annotation { "Feature Type Name" : "Feature", "Feature Type Description" : "" }
export const myFeature = defineFeature(function(context is Context, id is Id, definition is map)
    precondition{}
    {
        {
            var Q0;
            Q0=qCreatedBy(makeId("Top.planeOp"),FACE);
            var sketch = newSketch(context, id + "F0", { "sketchPlane" : qUnion([Q0])});
            skCircle(sketch, "E0", {"center": v(0, 0) * mm, "radius": 11 * mm});
            skCircle(sketch, "E1", {"center": v(0, 0) * mm, "radius": 13 * mm});
            skLineSegment(sketch, "E2", {"start": v(0, 0) * mm, "end": v(-13, 0) * mm});
            skArc(sketch, "E3", {"start": v(-13, 0) * mm, "mid": v(-12.77, 6.14) * mm, "end": v(-12.93, 12.28) * mm});
            skArc(sketch, "E4.MirrorCS", {"start": v(6.47, 11.28) * mm, "mid": v(1.06, 14.14) * mm, "end": v(-4.16, 17.34) * mm});
            skArc(sketch, "E5.1.0", {"start": v(6.5, -11.25) * mm, "mid": v(1.07, -14.12) * mm, "end": v(-4.17, -17.33) * mm});
            skArc(sketch, "E5.1.1", {"start": v(-13, -0.03) * mm, "mid": v(-12.78, -6.15) * mm, "end": v(-12.93, -12.28) * mm});
            skArc(sketch, "E5.2.0", {"start": v(6.5, 11.26) * mm, "mid": v(11.7, 7.99) * mm, "end": v(17.1, 5.05) * mm});
            skArc(sketch, "E5.2.1", {"start": v(6.53, -11.24) * mm, "mid": v(11.72, -7.98) * mm, "end": v(17.1, -5.05) * mm});
            skArc(sketch, "E6", {"start": v(-4.16, 17.34) * mm, "mid": v(-1.68, 23.22) * mm, "end": v(-2.3, 29.57) * mm});
            skCircle(sketch, "E7", {"center": v(-14.53, 25.18) * mm, "radius": 11 * mm});
            skCircle(sketch, "E8.1.0", {"center": v(-14.53, -25.18) * mm, "radius": 11 * mm});
            skArc(sketch, "E8.1.1", {"start": v(-12.93, -12.28) * mm, "mid": v(-19.27, -13.08) * mm, "end": v(-24.46, -16.8) * mm});
            skCircle(sketch, "E8.2.0", {"center": v(29.08, 0) * mm, "radius": 11 * mm});
            skArc(sketch, "E8.2.1", {"start": v(17.1, -5.05) * mm, "mid": v(20.95, -10.15) * mm, "end": v(26.76, -12.8) * mm});
            skPoint(sketch, "E9.orphan", {"position": v(-14.54, -25.16) * mm});
            skPoint(sketch, "E10.orphan", {"position": v(-14.55, -25.2) * mm});
            skPoint(sketch, "E11.orphan", {"position": v(-14.54, -25.18) * mm});
            skPoint(sketch, "E12.orphan", {"position": v(13, 0) * mm});
            skPoint(sketch, "E13.orphan", {"position": v(29.06, 0) * mm});
            skPoint(sketch, "E14.orphan", {"position": v(29.1, 0.02) * mm});
            skPoint(sketch, "E15.orphan", {"position": v(-6.5, 11.26) * mm});
            skPoint(sketch, "E16.orphan", {"position": v(-14.57, 25.2) * mm});
            skLineSegment(sketch, "E17", {"start": v(-14.53, 25.18) * mm, "end": v(-27.53, 25.18) * mm});
            skLineSegment(sketch, "E18", {"start": v(-27.53, 25.18) * mm, "end": v(-27.53, -25.18) * mm});
            skLineSegment(sketch, "E19", {"start": v(-24.46, 16.79) * mm, "end": v(-24.46, -16.8) * mm});
            skLineSegment(sketch, "E20.1.0", {"start": v(-8.04, -36.43) * mm, "end": v(35.57, -11.25) * mm});
            skLineSegment(sketch, "E20.1.1", {"start": v(-2.3, -29.58) * mm, "end": v(26.77, -12.79) * mm});
            skLineSegment(sketch, "E20.2.0", {"start": v(35.57, 11.25) * mm, "end": v(-8.04, 36.43) * mm});
            skLineSegment(sketch, "E20.2.1", {"start": v(26.77, 12.79) * mm, "end": v(-2.3, 29.57) * mm});
            skArc(sketch, "E21.trimOffspring", {"start": v(-24.46, 16.79) * mm, "mid": v(-19.26, 13.07) * mm, "end": v(-12.93, 12.28) * mm});
            skArc(sketch, "E22.trimOffspring", {"start": v(-27.53, -25.18) * mm, "mid": v(-20.78, -36.58) * mm, "end": v(-7.54, -36.14) * mm});
            skArc(sketch, "E23.trimOffspring", {"start": v(-2.3, -29.57) * mm, "mid": v(-1.68, -23.2) * mm, "end": v(-4.17, -17.33) * mm});
            skArc(sketch, "E24.trimOffspring", {"start": v(35.07, -11.54) * mm, "mid": v(42.08, -0.06) * mm, "end": v(35.17, 11.48) * mm});
            skArc(sketch, "E25.trimOffspring", {"start": v(26.77, 12.79) * mm, "mid": v(20.96, 10.14) * mm, "end": v(17.1, 5.05) * mm});
            skArc(sketch, "E26.trimOffspring", {"start": v(-7.63, 36.2) * mm, "mid": v(-20.83, 36.55) * mm, "end": v(-27.53, 25.18) * mm});
            skPoint(sketch, "E27.orphan", {"position": v(-2.31, 29.58) * mm});
            skCircle(sketch, "E28.cCircle", {"center": v(-14.53, -25.18) * mm, "radius": 6.35 * mm, "construction": true});
            skLineSegment(sketch, "E28.0", {"start": v(-14.82, -17.86) * mm, "end": v(-8.33, -21.27) * mm});
            skLineSegment(sketch, "E28.1", {"start": v(-8.33, -21.27) * mm, "end": v(-8.04, -28.6) * mm});
            skLineSegment(sketch, "E28.2", {"start": v(-8.04, -28.6) * mm, "end": v(-14.24, -32.51) * mm});
            skLineSegment(sketch, "E28.3", {"start": v(-14.24, -32.51) * mm, "end": v(-20.73, -29.1) * mm});
            skLineSegment(sketch, "E28.4", {"start": v(-20.73, -29.1) * mm, "end": v(-21.02, -21.77) * mm});
            skLineSegment(sketch, "E28.5", {"start": v(-21.02, -21.77) * mm, "end": v(-14.82, -17.86) * mm});
            skPoint(sketch, "E28.0.midPoint", {"position": v(-11.57, -19.56) * mm});
            skLineSegment(sketch, "E29.1.0", {"start": v(28.79, 7.33) * mm, "end": v(35.28, 3.92) * mm});
            skLineSegment(sketch, "E29.1.1", {"start": v(22.59, 3.42) * mm, "end": v(28.79, 7.33) * mm});
            skLineSegment(sketch, "E29.1.2", {"start": v(22.87, -3.9) * mm, "end": v(22.59, 3.42) * mm});
            skLineSegment(sketch, "E29.1.3", {"start": v(29.36, -7.32) * mm, "end": v(22.87, -3.9) * mm});
            skLineSegment(sketch, "E29.1.4", {"start": v(35.56, -3.4) * mm, "end": v(29.36, -7.32) * mm});
            skCircle(sketch, "E29.1.5", {"center": v(29.07, 0) * mm, "radius": 6.35 * mm, "construction": true});
            skLineSegment(sketch, "E29.1.6", {"start": v(35.28, 3.92) * mm, "end": v(35.56, -3.4) * mm});
            skLineSegment(sketch, "E29.2.0", {"start": v(-20.75, 21.26) * mm, "end": v(-21.03, 28.6) * mm});
            skLineSegment(sketch, "E29.2.1", {"start": v(-14.26, 17.85) * mm, "end": v(-20.75, 21.26) * mm});
            skLineSegment(sketch, "E29.2.2", {"start": v(-8.06, 21.76) * mm, "end": v(-14.26, 17.85) * mm});
            skLineSegment(sketch, "E29.2.3", {"start": v(-8.34, 29.09) * mm, "end": v(-8.06, 21.76) * mm});
            skLineSegment(sketch, "E29.2.4", {"start": v(-14.83, 32.5) * mm, "end": v(-8.34, 29.09) * mm});
            skCircle(sketch, "E29.2.5", {"center": v(-14.54, 25.18) * mm, "radius": 6.35 * mm, "construction": true});
            skLineSegment(sketch, "E29.2.6", {"start": v(-21.03, 28.6) * mm, "end": v(-14.83, 32.5) * mm});
            skLineSegment(sketch, "E30", {"start": v(-17.16, -30.98) * mm, "end": v(-17.15, -30.97) * mm});
            skPoint(sketch, "E31.orphan", {"position": v(-20.78, -36.58) * mm});
            skLineSegment(sketch, "E32.trimOffspring", {"start": v(-10.33, -20.42) * mm, "end": v(-10.24, -20.27) * mm});
            skLineSegment(sketch, "E33.trimOffspring", {"start": v(8.95, 9.43) * mm, "end": v(9.05, 9.6) * mm});
            skSolve(sketch);
        }
        {
            var Q0;
            {var subQ23=sQuery(id+"F0.wireOp",EDGE,"E6");Q0=makeQuery(id+"F0.imprint","IMPRINT",FACE,{"disambiguationData":[TD([[makeQuery(id+"F0.imprint","IMPRINT",EDGE,{"derivedFrom":subQ23}),1.0]])]});}
            var Q1;
            Q1=makeQuery(id+"F0.imprint","IMPRINT",FACE,{"disambiguationData":[TD([[makeQuery(id+"F0.imprint","IMPRINT",EDGE,{"derivedFrom":sQuery(id+"F0.wireOp",EDGE,"E0")}),-1.0]])]});
            var Q2;
            Q2=makeQuery(id+"F0.imprint","IMPRINT",FACE,{"disambiguationData":[TD([[makeQuery(id+"F0.imprint","IMPRINT",EDGE,{"derivedFrom":sQuery(id+"F0.wireOp",EDGE,"E8.1.0")}),1.0]])]});
            var Q3;
            Q3=makeQuery(id+"F0.imprint","IMPRINT",FACE,{"disambiguationData":[TD([[makeQuery(id+"F0.imprint","IMPRINT",EDGE,{"derivedFrom":sQuery(id+"F0.wireOp",EDGE,"E7")}),1.0]])]});
            var Q4;
            Q4=makeQuery(id+"F0.imprint","IMPRINT",FACE,{"disambiguationData":[TD([[makeQuery(id+"F0.imprint","IMPRINT",EDGE,{"derivedFrom":sQuery(id+"F0.wireOp",EDGE,"E8.2.0")}),1.0]])]});
            extrude(context, id + "F1", {"entities" : qUnion([Q0, Q1, Q2, Q3, Q4]), "depth" : 7 * mm, "offsetDistance" : 25 * mm});
        }
        {
            var Q0;
            Q0=makeQuery(id+"F1.opExtrude","SWEPT_FACE",FACE,{"disambiguationData":[OSD([sQuery(id+"F0.wireOp",EDGE,"E18")])]});
            var sketch = newSketch(context, id + "F2", { "sketchPlane" : qUnion([Q0])});
            skText(sketch, "E34", { "text": "WEBWAY VAPES", "fontName": "OpenSans-Regular.ttf"});
            const initialGuessF2  = {"E34": [-0.025, 0.00096, 1, 0, 0.00483]};
            skSetInitialGuess(sketch, initialGuessF2);
            skSolve(sketch);
        }
        {
            var Q0;
            Q0 = qSketchRegion(id + "F2", true);
            var Q1;
            Q1 = qConstructionFilter(qBodyType(qCreatedBy(id + "F2" ,EDGE), BodyType.WIRE), ConstructionObject.NO);
            extrude(context, id + "F3", {"entities" : qUnion([Q0]), "operationType" : NewBodyOperationType.REMOVE, "surfaceEntities" : qUnion([Q1]), "oppositeDirection" : true, "depth" : 1 * mm, "offsetDistance" : 25 * mm});
        }
        {
            var Q0;
            Q0=makeQuery(id+"F1.opExtrude","SWEPT_FACE",FACE,{"disambiguationData":[OSD([sQuery(id+"F0.wireOp",EDGE,"E20.2.0")])]});
            var sketch = newSketch(context, id + "F4", { "sketchPlane" : qUnion([Q0])});
            skText(sketch, "E35", { "text": "WEBWAY VAPES", "fontName": "OpenSans-Regular.ttf"});
            const initialGuessF4  = {"E35": [-0.02473, 0.00088, 1, 0, 0.00473]};
            skSetInitialGuess(sketch, initialGuessF4);
            skSolve(sketch);
        }
        {
            var Q0;
            Q0 = qSketchRegion(id + "F4", true);
            extrude(context, id + "F5", {"entities" : qUnion([Q0]), "operationType" : NewBodyOperationType.REMOVE, "oppositeDirection" : true, "depth" : 1 * mm, "offsetDistance" : 25 * mm});
        }
        {
            var Q0;
            Q0=makeQuery(id+"F1.opExtrude","SWEPT_FACE",FACE,{"disambiguationData":[OSD([sQuery(id+"F0.wireOp",EDGE,"E20.1.0")])]});
            var sketch = newSketch(context, id + "F6", { "sketchPlane" : qUnion([Q0])});
            skText(sketch, "E36", { "text": "WEBWAY VAPES", "fontName": "OpenSans-Regular.ttf"});
            const initialGuessF6  = {"E36": [-0.0245, 0.00092, 1, 0, 0.00473]};
            skSetInitialGuess(sketch, initialGuessF6);
            skSolve(sketch);
        }
        {
            var Q0;
            Q0 = qSketchRegion(id + "F6", true);
            extrude(context, id + "F7", {"entities" : qUnion([Q0]), "operationType" : NewBodyOperationType.REMOVE, "oppositeDirection" : true, "depth" : 1 * mm, "offsetDistance" : 25 * mm});
        }
    });